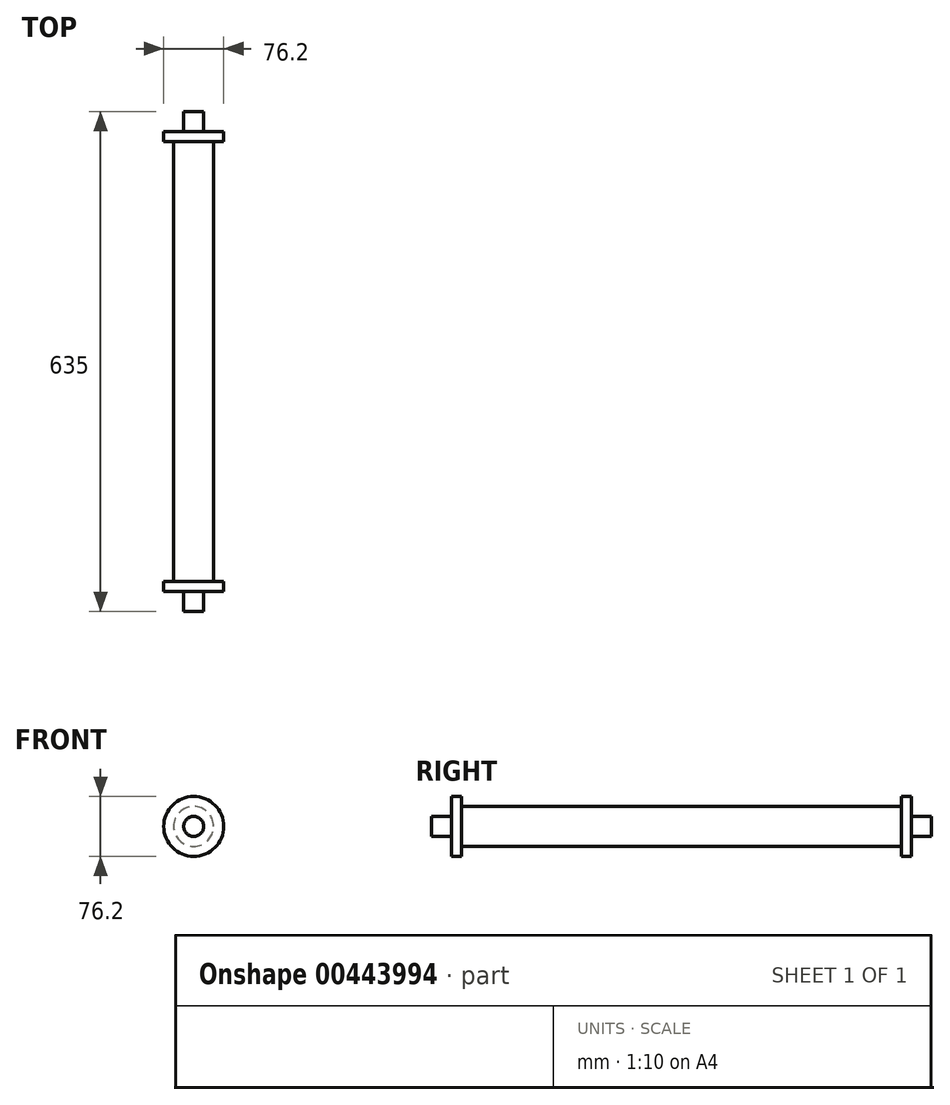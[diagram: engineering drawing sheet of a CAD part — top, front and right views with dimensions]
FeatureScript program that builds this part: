
annotation { "Feature Type Name" : "Feature", "Feature Type Description" : "" }
export const myFeature = defineFeature(function(context is Context, id is Id, definition is map)
    precondition{}
    {
        {
            var Q0;
            Q0=qCreatedBy(makeId("Front.planeOp"),FACE);
            var sketch = newSketch(context, id + "F0", { "sketchPlane" : qUnion([Q0])});
            skCircle(sketch, "E0", {"center": v(0, 0) * mm, "radius": 25.4 * mm});
            skSolve(sketch);
        }
        {
            var Q0;
            Q0=makeQuery(id+"F0.imprint","IMPRINT",FACE,{"disambiguationData":[TD([[makeQuery(id+"F0.imprint","IMPRINT",EDGE,{"derivedFrom":sQuery(id+"F0.wireOp",EDGE,"E0")}),1.0]])]});
            extrude(context, id + "F1", {"entities" : qUnion([Q0]), "depth" : 558.8 * mm});
        }
        {
            var Q0;
            Q0=makeQuery(id+"F1.opExtrude","CAP_FACE",FACE,{"disambiguationData":[OSD([sQuery(id+"F0.wireOp",EDGE,"E0")])],"isStart":false});
            var sketch = newSketch(context, id + "F2", { "sketchPlane" : qUnion([Q0])});
            skCircle(sketch, "E1", {"center": v(0, 0) * mm, "radius": 38.1 * mm});
            skSolve(sketch);
        }
        {
            var Q0;
            Q0=makeQuery(id+"F2.imprint","IMPRINT",FACE,{"disambiguationData":[TD([[makeQuery(id+"F2.imprint","IMPRINT",EDGE,{"derivedFrom":sQuery(id+"F2.wireOp",EDGE,"E1")}),1.0]])]});
            var Q1;
            Q1=makeQuery(id+"F2.imprint","IMPRINT",FACE,{"disambiguationData":[TD([[makeQuery(id+"F2.imprint","IMPRINT",EDGE,{"derivedFrom":makeQuery(id+"F1.opExtrude","CAP_EDGE",EDGE,{"disambiguationData":[OSD([sQuery(id+"F0.wireOp",EDGE,"E0")])],"isStart":false})}),1.0]])]});
            extrude(context, id + "F3", {"entities" : qUnion([Q0, Q1]), "operationType" : NewBodyOperationType.ADD, "depth" : 12.7 * mm});
        }
        {
            var Q0;
            Q0=makeQuery(id+"F1.opExtrude","CAP_FACE",FACE,{"disambiguationData":[OSD([sQuery(id+"F0.wireOp",EDGE,"E0")])],"isStart":true});
            var sketch = newSketch(context, id + "F4", { "sketchPlane" : qUnion([Q0])});
            skCircle(sketch, "E2", {"center": v(0, 0) * mm, "radius": 38.1 * mm});
            skSolve(sketch);
        }
        {
            var Q0;
            Q0=makeQuery(id+"F4.imprint","IMPRINT",FACE,{"disambiguationData":[TD([[makeQuery(id+"F4.imprint","IMPRINT",EDGE,{"derivedFrom":makeQuery(id+"F1.opExtrude","CAP_EDGE",EDGE,{"disambiguationData":[OSD([sQuery(id+"F0.wireOp",EDGE,"E0")])],"isStart":true})}),-1.0]])]});
            var Q1;
            Q1=makeQuery(id+"F4.imprint","IMPRINT",FACE,{"disambiguationData":[TD([[makeQuery(id+"F4.imprint","IMPRINT",EDGE,{"derivedFrom":sQuery(id+"F4.wireOp",EDGE,"E2")}),1.0]])]});
            extrude(context, id + "F5", {"entities" : qUnion([Q0, Q1]), "operationType" : NewBodyOperationType.ADD, "depth" : 12.7 * mm});
        }
        {
            var Q0;
            Q0=makeQuery(id+"F3.opExtrude","CAP_FACE",FACE,{"disambiguationData":[OSD([sQuery(id+"F2.wireOp",EDGE,"E1")])],"isStart":false});
            var sketch = newSketch(context, id + "F6", { "sketchPlane" : qUnion([Q0])});
            skCircle(sketch, "E3", {"center": v(0, 0) * mm, "radius": 12.7 * mm});
            skSolve(sketch);
        }
        {
            var Q0;
            Q0=makeQuery(id+"F5.opExtrude","CAP_FACE",FACE,{"disambiguationData":[OSD([sQuery(id+"F4.wireOp",EDGE,"E2")])],"isStart":false});
            var sketch = newSketch(context, id + "F7", { "sketchPlane" : qUnion([Q0])});
            skCircle(sketch, "E4", {"center": v(0, 0) * mm, "radius": 12.7 * mm});
            skSolve(sketch);
        }
        {
            var Q0;
            Q0=makeQuery(id+"F7.imprint","IMPRINT",FACE,{"disambiguationData":[TD([[makeQuery(id+"F7.imprint","IMPRINT",EDGE,{"derivedFrom":sQuery(id+"F7.wireOp",EDGE,"E4")}),1.0]])]});
            var Q1;
            Q1=makeQuery(id+"F6.imprint","IMPRINT",FACE,{"disambiguationData":[TD([[makeQuery(id+"F6.imprint","IMPRINT",EDGE,{"derivedFrom":sQuery(id+"F6.wireOp",EDGE,"E3")}),1.0]])]});
            extrude(context, id + "F8", {"entities" : qUnion([Q0, Q1]), "operationType" : NewBodyOperationType.ADD, "depth" : 25.4 * mm, "hasSecondDirection" : true, "secondDirectionOppositeDirection" : true, "secondDirectionDepth" : 25.4 * mm});
        }
    });
